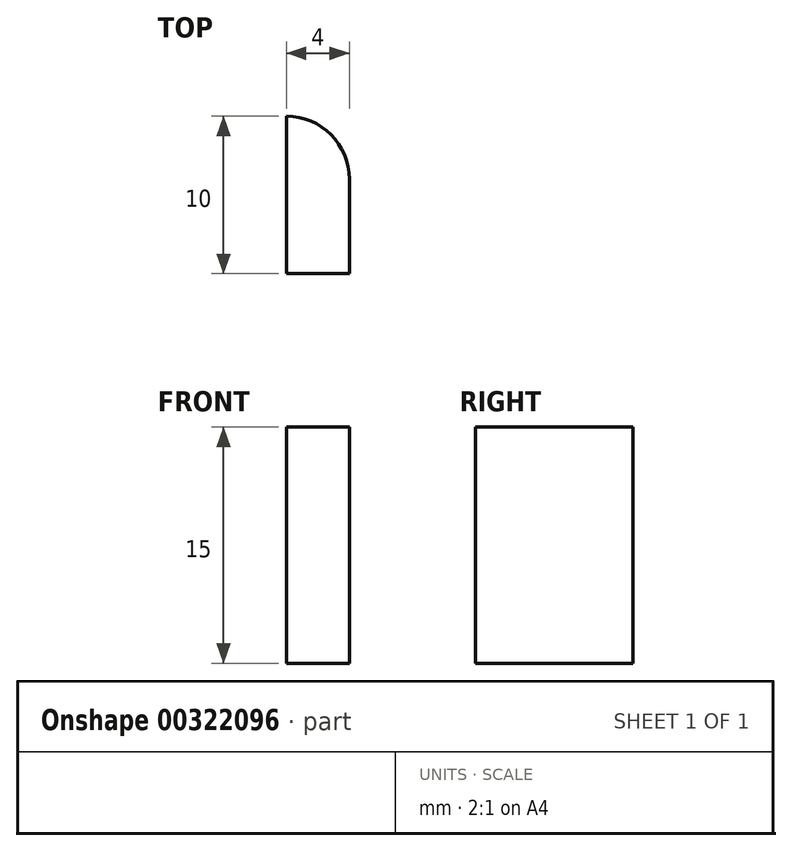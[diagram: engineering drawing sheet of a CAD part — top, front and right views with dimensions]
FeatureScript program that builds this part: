
annotation { "Feature Type Name" : "Feature", "Feature Type Description" : "" }
export const myFeature = defineFeature(function(context is Context, id is Id, definition is map)
    precondition{}
    {
        {
            var Q0;
            Q0=qCreatedBy(makeId("Top.planeOp"),FACE);
            var sketch = newSketch(context, id + "F0", { "sketchPlane" : qUnion([Q0])});
            skArc(sketch, "E0", {"start": v(4, 0) * mm, "mid": v(2.83, 2.83) * mm, "end": v(0, 4) * mm});
            skLineSegment(sketch, "E1", {"start": v(0, 0) * mm, "end": v(0, 4) * mm});
            skLineSegment(sketch, "E2.top", {"start": v(0, -6) * mm, "end": v(4, -6) * mm});
            skLineSegment(sketch, "E2.left", {"start": v(0, 0) * mm, "end": v(0, -6) * mm});
            skLineSegment(sketch, "E2.right", {"start": v(4, 0) * mm, "end": v(4, -6) * mm});
            skSolve(sketch);
        }
        {
            var Q0;
            Q0 = qSketchRegion(id + "F0", true);
            extrude(context, id + "F1", {"entities" : qUnion([Q0]), "depth" : 15 * mm});
        }
    });
